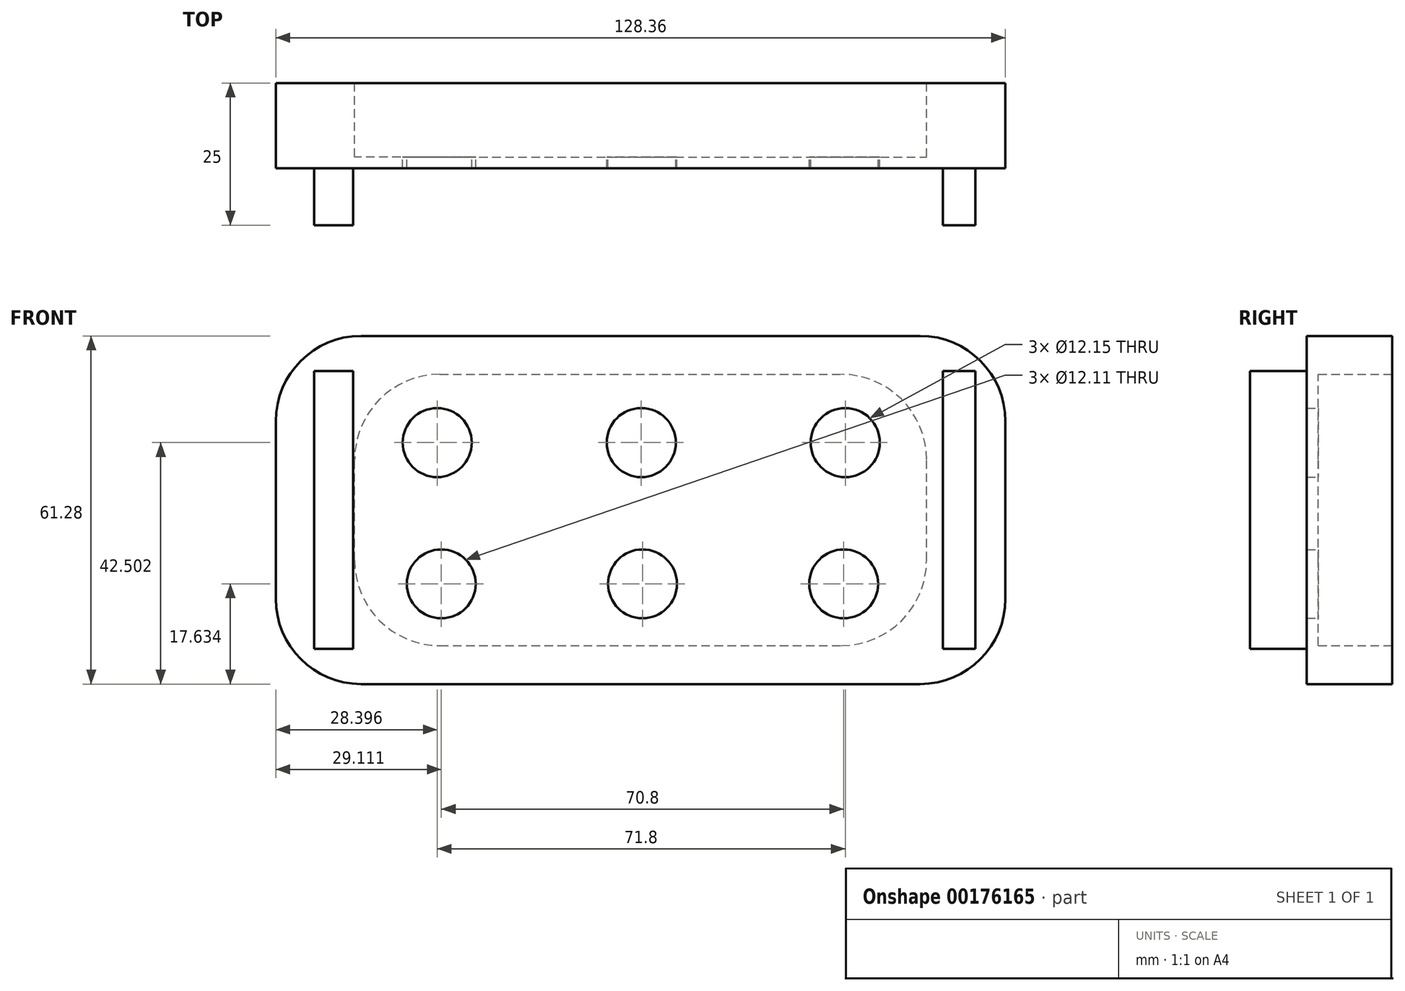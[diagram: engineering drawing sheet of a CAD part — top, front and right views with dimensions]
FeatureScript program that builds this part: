
annotation { "Feature Type Name" : "Feature", "Feature Type Description" : "" }
export const myFeature = defineFeature(function(context is Context, id is Id, definition is map)
    precondition{}
    {
        {
            var Q0;
            Q0=qCreatedBy(makeId("Front.planeOp"),FACE);
            var sketch = newSketch(context, id + "F0", { "sketchPlane" : qUnion([Q0])});
            skLineSegment(sketch, "E0.bottom", {"start": v(-49.18, -30.64) * mm, "end": v(49.18, -30.64) * mm});
            skLineSegment(sketch, "E0.top", {"start": v(-49.18, 30.64) * mm, "end": v(49.18, 30.64) * mm});
            skLineSegment(sketch, "E0.left", {"start": v(-64.18, -15.64) * mm, "end": v(-64.18, 15.64) * mm});
            skLineSegment(sketch, "E0.right", {"start": v(64.18, -15.64) * mm, "end": v(64.18, 15.64) * mm});
            skPoint(sketch, "E0.middle", {"position": v(0, 0) * mm});
            skPoint(sketch, "E1.visualSharp", {"position": v(-64.18, 30.64) * mm});
            skArc(sketch, "E1.filletArc", {"start": v(-49.18, 30.64) * mm, "mid": v(-59.79, 26.25) * mm, "end": v(-64.18, 15.64) * mm});
            skPoint(sketch, "E2.visualSharp", {"position": v(-64.18, -30.64) * mm});
            skArc(sketch, "E2.filletArc", {"start": v(-64.18, -15.64) * mm, "mid": v(-59.79, -26.25) * mm, "end": v(-49.18, -30.64) * mm});
            skPoint(sketch, "E3.visualSharp", {"position": v(64.18, -30.64) * mm});
            skArc(sketch, "E3.filletArc", {"start": v(49.18, -30.64) * mm, "mid": v(59.79, -26.25) * mm, "end": v(64.18, -15.64) * mm});
            skPoint(sketch, "E4.visualSharp", {"position": v(64.18, 30.64) * mm});
            skArc(sketch, "E4.filletArc", {"start": v(64.18, 15.64) * mm, "mid": v(59.79, 26.25) * mm, "end": v(49.18, 30.64) * mm});
            skSolve(sketch);
        }
        {
            var Q0;
            Q0=makeQuery(id+"F0.imprint","IMPRINT",FACE,{"disambiguationData":[TD([[makeQuery(id+"F0.imprint","IMPRINT",EDGE,{"derivedFrom":sQuery(id+"F0.wireOp",EDGE,"E0.bottom")}),1.0]])]});
            extrude(context, id + "F1", {"entities" : qUnion([Q0]), "depth" : 15 * mm});
        }
        {
            var Q0;
            Q0=qCreatedBy(makeId("Front.planeOp"),FACE);
            var sketch = newSketch(context, id + "F2", { "sketchPlane" : qUnion([Q0])});
            skLineSegment(sketch, "E5.bottom", {"start": v(-35.3, -23.87) * mm, "end": v(35.3, -23.87) * mm});
            skLineSegment(sketch, "E5.top", {"start": v(-35.3, 23.87) * mm, "end": v(35.3, 23.87) * mm});
            skLineSegment(sketch, "E5.left", {"start": v(-50.3, -8.87) * mm, "end": v(-50.3, 8.87) * mm});
            skLineSegment(sketch, "E5.right", {"start": v(50.3, -8.87) * mm, "end": v(50.3, 8.87) * mm});
            skPoint(sketch, "E5.middle", {"position": v(0, 0) * mm});
            skPoint(sketch, "E6.visualSharp", {"position": v(50.3, 23.87) * mm});
            skArc(sketch, "E6.filletArc", {"start": v(50.3, 8.87) * mm, "mid": v(45.92, 19.47) * mm, "end": v(35.3, 23.87) * mm});
            skPoint(sketch, "E7.visualSharp", {"position": v(50.3, -23.87) * mm});
            skArc(sketch, "E7.filletArc", {"start": v(35.3, -23.87) * mm, "mid": v(45.92, -19.47) * mm, "end": v(50.3, -8.87) * mm});
            skPoint(sketch, "E8.visualSharp", {"position": v(-50.3, -23.87) * mm});
            skArc(sketch, "E8.filletArc", {"start": v(-50.3, -8.87) * mm, "mid": v(-45.92, -19.47) * mm, "end": v(-35.3, -23.87) * mm});
            skPoint(sketch, "E9.visualSharp", {"position": v(-50.3, 23.87) * mm});
            skArc(sketch, "E9.filletArc", {"start": v(-35.3, 23.87) * mm, "mid": v(-45.92, 19.47) * mm, "end": v(-50.3, 8.87) * mm});
            skSolve(sketch);
        }
        {
            var Q0;
            Q0=makeQuery(id+"F2.imprint","IMPRINT",FACE,{"disambiguationData":[TD([[makeQuery(id+"F2.imprint","IMPRINT",EDGE,{"derivedFrom":sQuery(id+"F2.wireOp",EDGE,"E5.bottom")}),1.0]])]});
            extrude(context, id + "F3", {"entities" : qUnion([Q0]), "operationType" : NewBodyOperationType.REMOVE, "depth" : 13 * mm});
        }
        {
            var Q0;
            Q0=makeQuery(id+"F3.boolean.opBoolean","COPY",FACE,{"derivedFrom":makeQuery(id+"F3.opExtrude","CAP_FACE",FACE,{"disambiguationData":[OSD([sQuery(id+"F2.wireOp",EDGE,"E5.bottom"),sQuery(id+"F2.wireOp",EDGE,"E5.top"),sQuery(id+"F2.wireOp",EDGE,"E5.left"),sQuery(id+"F2.wireOp",EDGE,"E5.right"),sQuery(id+"F2.wireOp",EDGE,"E6.filletArc"),sQuery(id+"F2.wireOp",EDGE,"E7.filletArc"),sQuery(id+"F2.wireOp",EDGE,"E8.filletArc"),sQuery(id+"F2.wireOp",EDGE,"E9.filletArc")])],"isStart":false})});
            var sketch = newSketch(context, id + "F4", { "sketchPlane" : qUnion([Q0])});
            skCircle(sketch, "E10", {"center": v(-36.02, 11.86) * mm, "radius": 6.08 * mm});
            skCircle(sketch, "E11.1.0.0", {"center": v(-0.12, 11.86) * mm, "radius": 6.08 * mm});
            skCircle(sketch, "E11.2.0.0", {"center": v(35.78, 11.86) * mm, "radius": 6.08 * mm});
            skLineSegment(sketch, "E11.direction1", {"start": v(-36.02, 11.86) * mm, "end": v(-0.12, 11.86) * mm, "construction": true});
            skCircle(sketch, "E12", {"center": v(-35.73, -13) * mm, "radius": 6.06 * mm});
            skCircle(sketch, "E13.1.0.0", {"center": v(-0.33, -13) * mm, "radius": 6.06 * mm});
            skCircle(sketch, "E13.2.0.0", {"center": v(35.07, -13) * mm, "radius": 6.06 * mm});
            skLineSegment(sketch, "E13.direction1", {"start": v(-35.73, -13) * mm, "end": v(-0.33, -13) * mm, "construction": true});
            skSolve(sketch);
        }
        {
            var Q0;
            Q0 = qSketchRegion(id + "F4", true);
            extrude(context, id + "F5", {"entities" : qUnion([Q0]), "operationType" : NewBodyOperationType.REMOVE, "endBound" : BoundingType.THROUGH_ALL, "oppositeDirection" : true, "depth" : 25 * mm});
        }
        {
            var Q0;
            Q0=qCreatedBy(makeId("Front.planeOp"),FACE);
            var sketch = newSketch(context, id + "F6", { "sketchPlane" : qUnion([Q0])});
            skLineSegment(sketch, "E14.bottom", {"start": v(-57.45, -24.44) * mm, "end": v(-50.6, -24.44) * mm});
            skLineSegment(sketch, "E14.top", {"start": v(-57.45, 24.44) * mm, "end": v(-50.6, 24.44) * mm});
            skLineSegment(sketch, "E14.left", {"start": v(-57.45, -24.44) * mm, "end": v(-57.45, 24.44) * mm});
            skLineSegment(sketch, "E14.right", {"start": v(-50.6, -24.44) * mm, "end": v(-50.6, 24.44) * mm});
            skPoint(sketch, "E14.middle", {"position": v(-54.02, 0) * mm});
            skLineSegment(sketch, "E15.bottom", {"start": v(53.17, -24.44) * mm, "end": v(58.88, -24.44) * mm});
            skLineSegment(sketch, "E15.top", {"start": v(53.17, 24.44) * mm, "end": v(58.88, 24.44) * mm});
            skLineSegment(sketch, "E15.left", {"start": v(53.17, -24.44) * mm, "end": v(53.17, 24.44) * mm});
            skLineSegment(sketch, "E15.right", {"start": v(58.88, -24.44) * mm, "end": v(58.88, 24.44) * mm});
            skPoint(sketch, "E15.middle", {"position": v(56.03, 0) * mm});
            skPoint(sketch, "E15.cornerSnap0", {"position": v(-54.02, -24.44) * mm});
            skSolve(sketch);
        }
        {
            var Q0;
            Q0 = qSketchRegion(id + "F6", true);
            extrude(context, id + "F7", {"entities" : qUnion([Q0]), "operationType" : NewBodyOperationType.ADD, "depth" : 25 * mm});
        }
    });
